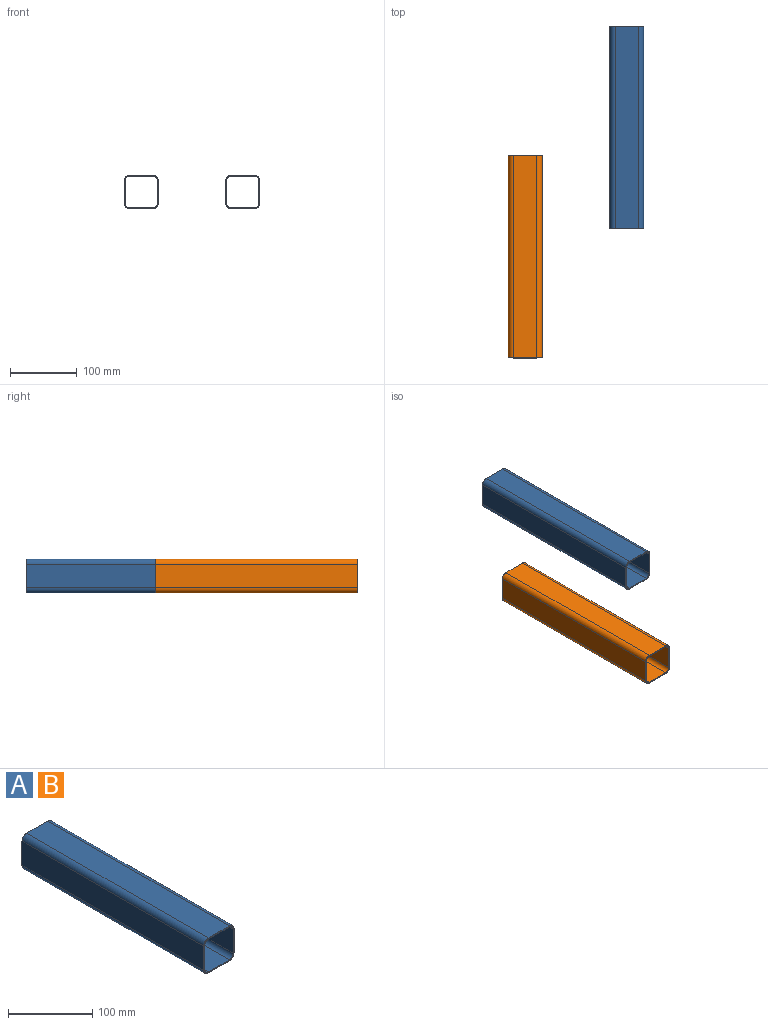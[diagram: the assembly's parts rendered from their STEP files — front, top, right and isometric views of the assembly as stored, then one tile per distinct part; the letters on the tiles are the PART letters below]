
ASSEMBLY  parts=2 mates=1
PART A: 18 faces, bbox 50.8x304.8x50.8 mm
  f0: plane 304.8x35.05mm, normal (1,0,0), area 10683.8mm2, adj f1,f15,f16,f17
  f1: cylinder r=7.87mm len=304.8mm, axis (0,1,0), area 3769.9mm2, adj f0,f2,f16,f17
  f2: plane 304.8x35.05mm, normal (0,0,1), area 10683.8mm2, adj f1,f3,f16,f17
  f3: cylinder r=7.87mm len=304.8mm, axis (0,1,0), area 3769.9mm2, adj f2,f4,f16,f17
  f4: plane 304.8x35.05mm, normal (-1,0,0), area 10683.8mm2, adj f3,f5,f16,f17
  f5: cylinder r=7.87mm len=304.8mm, axis (0,1,0), area 3769.9mm2, adj f4,f6,f16,f17
  f6: plane 304.8x35.05mm, normal (0,0,-1), area 10683.8mm2, adj f5,f15,f16,f17
  f7: cylinder r=6.35mm len=304.8mm, axis (0,1,0), area 3040.2mm2, adj f8,f14,f16,f17
  f8: plane 304.8x35.05mm, normal (-1,0,0), area 10683.8mm2, adj f7,f9,f16,f17
  f9: cylinder r=6.35mm len=304.8mm, axis (0,1,0), area 3040.2mm2, adj f8,f10,f16,f17
  f10: plane 304.8x35.05mm, normal (0,0,1), area 10683.8mm2, adj f9,f11,f16,f17
  f11: cylinder r=6.35mm len=304.8mm, axis (0,1,0), area 3040.2mm2, adj f10,f12,f16,f17
  f12: plane 304.8x35.05mm, normal (1,0,0), area 10683.8mm2, adj f11,f13,f16,f17
  f13: cylinder r=6.35mm len=304.8mm, axis (0,1,0), area 3040.2mm2, adj f12,f14,f16,f17
  f14: plane 304.8x35.05mm, normal (0,0,-1), area 10683.8mm2, adj f7,f13,f16,f17
  f15: cylinder r=7.87mm len=304.8mm, axis (0,1,0), area 3769.9mm2, adj f0,f6,f16,f17
  f16: plane 50.8x50.8mm, normal (0,-1,0), area 281.8mm2, adj f0,f1,f2,f3,f4,f5,f6,f7
  f17: plane 50.8x50.8mm, normal (0,1,0), area 281.8mm2, adj f0,f1,f2,f3,f4,f5,f6,f7
PART B: same geometry as A
PLACE A t=(101.11,45.81,34.02)mm
PLACE B t=(-51.19,-148.19,34.02)mm
MATE planar B.f2 <-> A.f2  axis (0,0,1) through (-51.19,-148.19,59.42)mm
